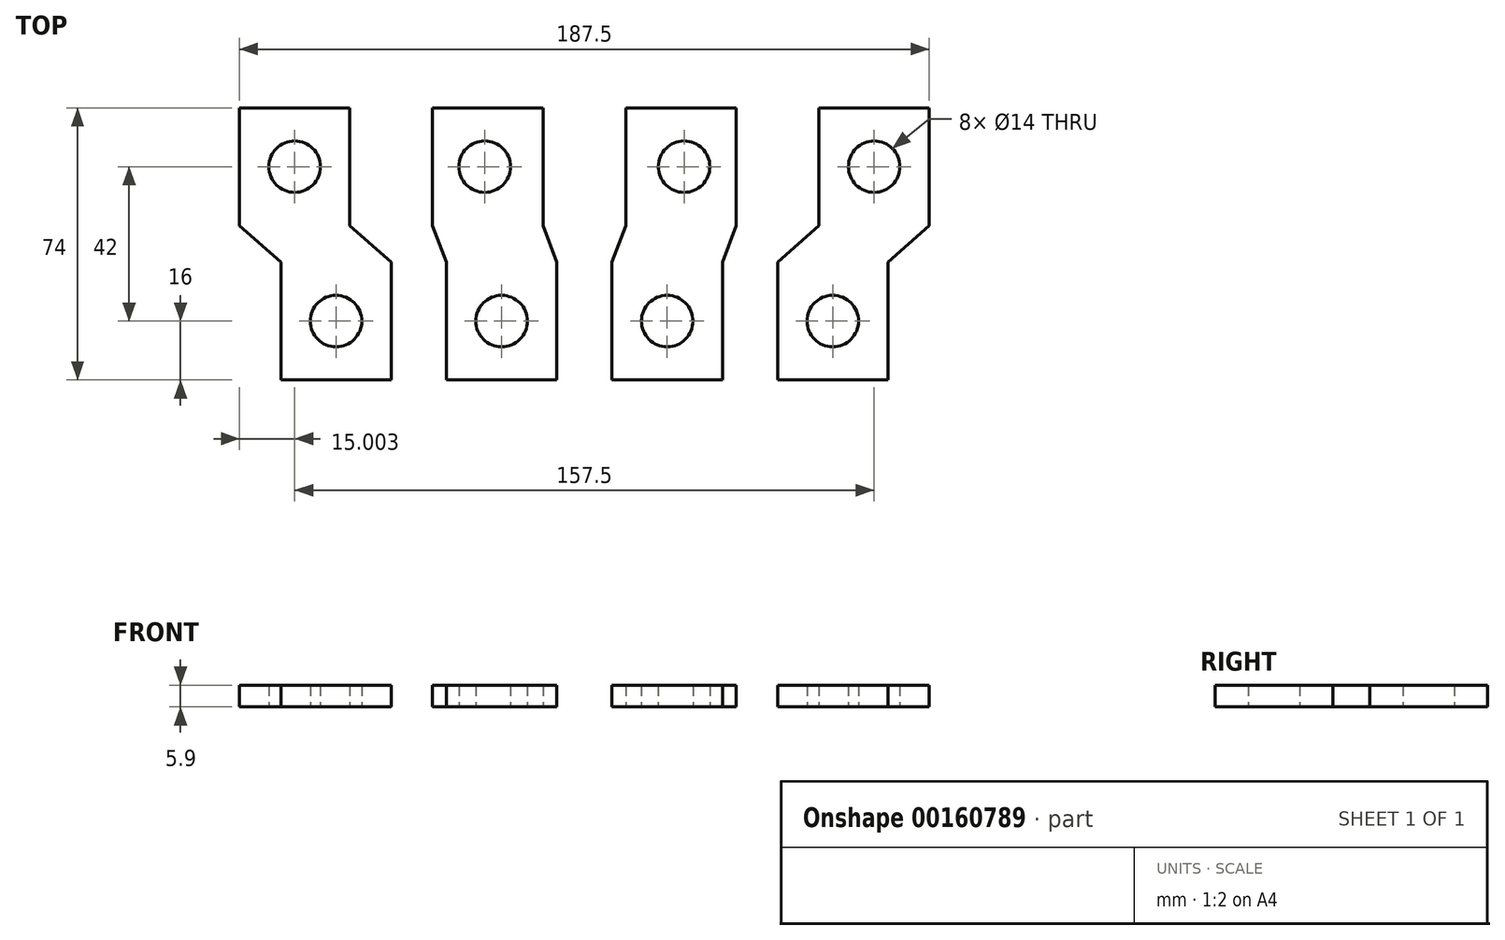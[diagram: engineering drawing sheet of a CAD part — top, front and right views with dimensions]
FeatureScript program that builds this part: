
annotation { "Feature Type Name" : "Feature", "Feature Type Description" : "" }
export const myFeature = defineFeature(function(context is Context, id is Id, definition is map)
    precondition{}
    {
        {
            var Q0;
            Q0=qCreatedBy(makeId("Top.planeOp"),FACE);
            var sketch = newSketch(context, id + "F0", { "sketchPlane" : qUnion([Q0])});
            skLineSegment(sketch, "E0.top", {"start": v(15.84, 37) * mm, "end": v(-14.16, 37) * mm});
            skLineSegment(sketch, "E0.right", {"start": v(-14.16, 5) * mm, "end": v(-14.16, 37) * mm});
            skLineSegment(sketch, "E1.bottom", {"start": v(-36.66, 37) * mm, "end": v(-66.66, 37) * mm});
            skCircle(sketch, "E2", {"center": v(0, 21) * mm, "radius": 7 * mm});
            skCircle(sketch, "E3", {"center": v(-51.66, 21) * mm, "radius": 7 * mm});
            skPoint(sketch, "E3.centerSnap0", {"position": v(-51.66, 37) * mm});
            skLineSegment(sketch, "E4", {"start": v(-55.4, -37) * mm, "end": v(-25.4, -37) * mm});
            skLineSegment(sketch, "E5.left", {"start": v(-25.4, -5) * mm, "end": v(-25.4, -37) * mm});
            skLineSegment(sketch, "E5.right", {"start": v(-55.4, -5) * mm, "end": v(-55.4, -37) * mm});
            skLineSegment(sketch, "E6.left", {"start": v(19.6, -5) * mm, "end": v(19.6, -37) * mm});
            skLineSegment(sketch, "E6.right", {"start": v(-10.4, -5) * mm, "end": v(-10.4, -37) * mm});
            skLineSegment(sketch, "E7", {"start": v(-66.66, 37) * mm, "end": v(-36.66, 37) * mm});
            skLineSegment(sketch, "E8", {"start": v(-55.4, -5) * mm, "end": v(-66.66, 5) * mm});
            skLineSegment(sketch, "E9", {"start": v(-25.4, -5) * mm, "end": v(-36.66, 5) * mm});
            skLineSegment(sketch, "E10", {"start": v(-10.4, -5) * mm, "end": v(-14.16, 5) * mm});
            skLineSegment(sketch, "E11", {"start": v(19.6, -5) * mm, "end": v(15.84, 5) * mm});
            skLineSegment(sketch, "E12", {"start": v(-66.66, 5) * mm, "end": v(-66.66, 37) * mm});
            skLineSegment(sketch, "E13", {"start": v(-36.66, 5) * mm, "end": v(-36.66, 37) * mm});
            skLineSegment(sketch, "E14.trimOffspring", {"start": v(-14.16, 37) * mm, "end": v(15.84, 37) * mm});
            skLineSegment(sketch, "E15.trimOffspring", {"start": v(-10.4, -37) * mm, "end": v(19.6, -37) * mm});
            skLineSegment(sketch, "E16", {"start": v(-40.4, -37) * mm, "end": v(-40.4, -21) * mm});
            skCircle(sketch, "E17", {"center": v(-40.4, -21) * mm, "radius": 7 * mm});
            skCircle(sketch, "E18.1.0.0", {"center": v(4.6, -21) * mm, "radius": 7 * mm});
            skLineSegment(sketch, "E19.trimOffspring", {"start": v(15.84, 5) * mm, "end": v(15.84, 37) * mm});
            skLineSegment(sketch, "E20.MirrorCS", {"start": v(90.84, 37) * mm, "end": v(120.84, 37) * mm});
            skLineSegment(sketch, "E21.MirrorCS", {"start": v(68.34, 37) * mm, "end": v(38.34, 37) * mm});
            skLineSegment(sketch, "E22.MirrorCS", {"start": v(90.84, 5) * mm, "end": v(90.84, 37) * mm});
            skLineSegment(sketch, "E23.MirrorCS", {"start": v(38.34, 5) * mm, "end": v(38.34, 37) * mm});
            skCircle(sketch, "E24.MirrorC", {"center": v(105.84, 21) * mm, "radius": 7 * mm});
            skCircle(sketch, "E25.MirrorC", {"center": v(49.6, -21) * mm, "radius": 7 * mm});
            skLineSegment(sketch, "E26.MirrorCS", {"start": v(120.84, 37) * mm, "end": v(90.84, 37) * mm});
            skLineSegment(sketch, "E27.MirrorCS", {"start": v(109.6, -5) * mm, "end": v(109.6, -37) * mm});
            skLineSegment(sketch, "E28.MirrorCS", {"start": v(64.6, -5) * mm, "end": v(64.6, -37) * mm});
            skLineSegment(sketch, "E29.MirrorCS", {"start": v(34.6, -5) * mm, "end": v(34.6, -37) * mm});
            skLineSegment(sketch, "E30.MirrorCS", {"start": v(79.6, -5) * mm, "end": v(90.84, 5) * mm});
            skLineSegment(sketch, "E31.MirrorCS", {"start": v(34.6, -5) * mm, "end": v(38.34, 5) * mm});
            skCircle(sketch, "E32.MirrorC", {"center": v(94.6, -21) * mm, "radius": 7 * mm});
            skLineSegment(sketch, "E33.MirrorCS", {"start": v(68.34, 5) * mm, "end": v(68.34, 37) * mm});
            skLineSegment(sketch, "E34.MirrorCS", {"start": v(120.84, 5) * mm, "end": v(120.84, 37) * mm});
            skLineSegment(sketch, "E35.MirrorCS", {"start": v(79.6, -5) * mm, "end": v(79.6, -37) * mm});
            skLineSegment(sketch, "E36.MirrorCS", {"start": v(64.6, -5) * mm, "end": v(68.34, 5) * mm});
            skPoint(sketch, "E37.MirrorP", {"position": v(105.84, 37) * mm});
            skLineSegment(sketch, "E38.MirrorCS", {"start": v(64.6, -37) * mm, "end": v(34.6, -37) * mm});
            skCircle(sketch, "E39.MirrorC", {"center": v(54.19, 21) * mm, "radius": 7 * mm});
            skLineSegment(sketch, "E40.MirrorCS", {"start": v(109.6, -5) * mm, "end": v(120.84, 5) * mm});
            skLineSegment(sketch, "E41.MirrorCS", {"start": v(109.6, -37) * mm, "end": v(79.6, -37) * mm});
            skLineSegment(sketch, "E42.MirrorCS", {"start": v(38.34, 37) * mm, "end": v(68.34, 37) * mm});
            skSolve(sketch);
        }
        {
            var Q0;
            Q0=makeQuery(id+"F0.imprint","IMPRINT",FACE,{"disambiguationData":[TD([[makeQuery(id+"F0.imprint","IMPRINT",EDGE,{"derivedFrom":sQuery(id+"F0.wireOp",EDGE,"E3")}),-1.0]])]});
            var Q1;
            Q1=makeQuery(id+"F0.imprint","IMPRINT",FACE,{"disambiguationData":[TD([[makeQuery(id+"F0.imprint","IMPRINT",EDGE,{"derivedFrom":sQuery(id+"F0.wireOp",EDGE,"E0.right")}),-1.0]])]});
            var Q2;
            Q2=makeQuery(id+"F0.imprint","IMPRINT",FACE,{"disambiguationData":[TD([[makeQuery(id+"F0.imprint","IMPRINT",EDGE,{"derivedFrom":sQuery(id+"F0.wireOp",EDGE,"E23.MirrorCS")}),-1.0]])]});
            var Q3;
            Q3=makeQuery(id+"F0.imprint","IMPRINT",FACE,{"disambiguationData":[TD([[makeQuery(id+"F0.imprint","IMPRINT",EDGE,{"derivedFrom":sQuery(id+"F0.wireOp",EDGE,"E22.MirrorCS")}),-1.0]])]});
            extrude(context, id + "F1", {"entities" : qUnion([Q0, Q1, Q2, Q3]), "depth" : 5.9 * mm});
        }
    });
